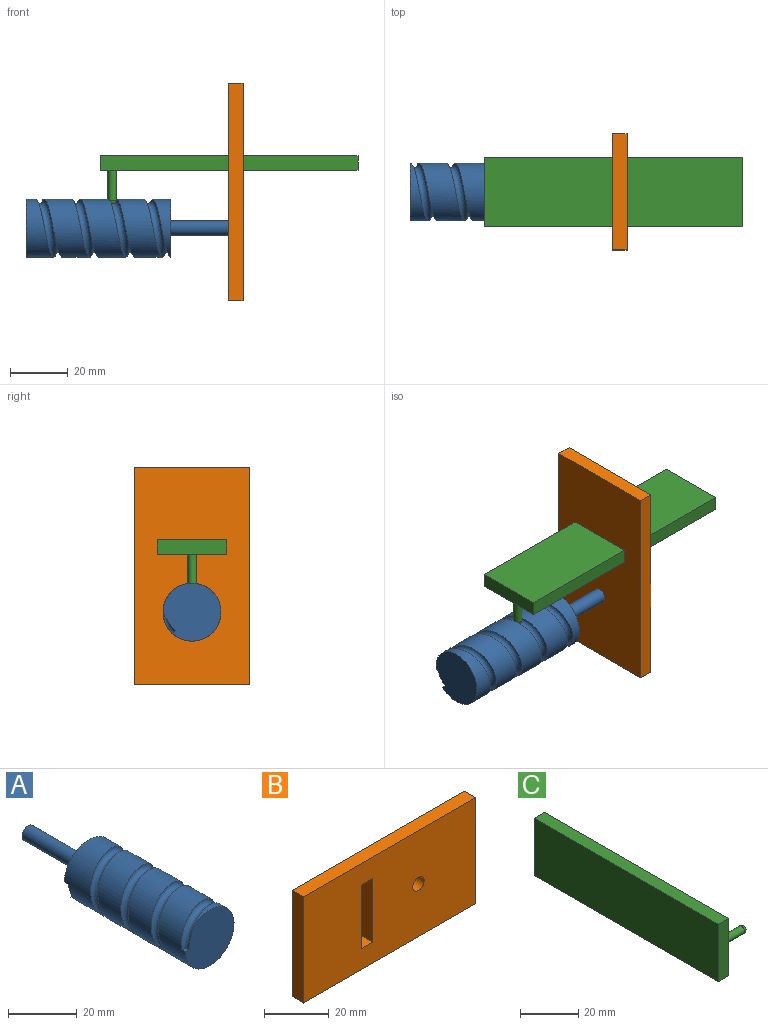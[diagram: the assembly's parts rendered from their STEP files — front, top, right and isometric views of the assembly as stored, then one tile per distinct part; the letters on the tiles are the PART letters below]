
ASSEMBLY  parts=3 mates=2
PART A: 8 faces, bbox 20x76.5x20 mm
  f0: plane 20x20mm, normal (0,-1,0), area 305.9mm2, adj f1,f3,f5
  f1: cylinder r=10mm len=50mm, axis (0,1,0), area 2394.3mm2, adj f0,f2,f3,f4,f5
  f2: plane 20x20mm, normal (0,1,0), area 286.2mm2, adj f1,f4,f5,f6
  f3: plane 1.5x1.5mm, normal (0,0,1), area 1.8mm2, adj f0,f1,f5
  f4: plane 1.5x1.5mm, normal (0,0,-1), area 1.8mm2, adj f1,f2,f5
  f5: bspline ~53x19.99mm, area 1063.1mm2, adj f0,f1,f2,f3,f4
  f6: cylinder r=2.5mm len=25mm, axis (0,-1,0), area 392.7mm2, adj f2,f7
  f7: plane 5x5mm, normal (0,1,0), area 19.6mm2, adj f6
PART B: 11 faces, bbox 75x5x40 mm
  f0: plane 75x40mm, normal (0,-1,0), area 2860.4mm2, adj f2,f3,f4,f5,f6,f7,f8,f9
  f1: plane 75x40mm, normal (0,1,0), area 2860.4mm2, adj f2,f3,f4,f5,f6,f7,f8,f9
  f2: plane 40x5mm, normal (1,0,0), area 200mm2, adj f0,f1,f3,f5
  f3: plane 75x5mm, normal (0,0,-1), area 375mm2, adj f0,f1,f2,f4
  f4: plane 40x5mm, normal (-1,0,0), area 200mm2, adj f0,f1,f3,f5
  f5: plane 75x5mm, normal (0,0,1), area 375mm2, adj f0,f1,f2,f4
  f6: cylinder r=2.5mm len=5mm, axis (0,1,0), area 78.5mm2, adj f0,f1
  f7: plane 24x5mm, normal (-1,0,0), area 120mm2, adj f0,f1,f8,f10
  f8: plane 5x5mm, normal (0,0,1), area 25mm2, adj f0,f1,f7,f9
  f9: plane 24x5mm, normal (1,0,0), area 120mm2, adj f0,f1,f8,f10
  f10: plane 5x5mm, normal (0,0,-1), area 25mm2, adj f0,f1,f7,f9
PART C: 8 faces, bbox 17x89.1x24 mm
  f0: plane 89.1x24mm, normal (1,0,0), area 2131.3mm2, adj f1,f3,f4,f5,f6
  f1: plane 89.1x5mm, normal (0,0,-1), area 445.5mm2, adj f0,f2,f4,f5
  f2: plane 89.1x24mm, normal (-1,0,0), area 2138.4mm2, adj f1,f3,f4,f5
  f3: plane 89.1x5mm, normal (0,0,1), area 445.5mm2, adj f0,f2,f4,f5
  f4: plane 24x5mm, normal (0,-1,0), area 120mm2, adj f0,f1,f2,f3
  f5: plane 24x5mm, normal (0,1,0), area 120mm2, adj f0,f1,f2,f3
  f6: cylinder r=1.5mm len=10.5mm, axis (-1,0,0), area 99mm2, adj f0,f7
  f7: sphere r=1.5mm, area 14.1mm2, adj f6
PLACE A rot(axis=(-0.38,-0.38,-0.85),99.5deg) t=(-47.5,0,25)mm
PLACE B rot(axis=(0.58,0.58,-0.58),120deg) t=(-47.5,0,25)mm fixed
PLACE C rot(axis=(0.58,0.58,-0.58),120deg) t=(-7.77,0,25)mm
MATE revolute A.f6 <-> B.f6  axis (-1,0,0) through (2.5,0,25)mm
MATE slider C.f5 <-> B.f1  axis (1,0,0) through (42.23,0,47.5)mm
